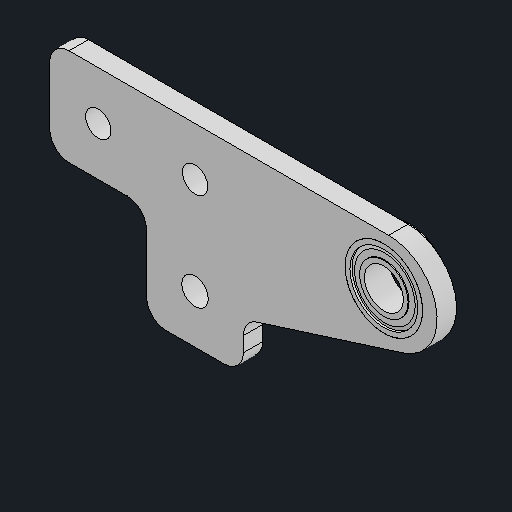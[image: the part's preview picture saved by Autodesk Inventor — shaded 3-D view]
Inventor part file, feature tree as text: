
AUTODESK INVENTOR PART (.ipt)
format: ipt  version: 2024.2 (Build 282272000, 272)  size: 135,168 bytes
history: native  units: mm
features: other x3, fillet x1
ambient origin geometry x8: Origin, YZ Plane, XZ Plane, XY Plane, X Axis, Y Axis, Z Axis, Center Point
bodies: Body1 (feature_tree), Body2 (feature_tree)
feature tree (4):
  other  "솔리드1"
  other  "솔리드2"
  fillet  "Fillet1"  [1 undecoded]
  other  "Cut-Revolve1"
note: 1 required parameter value undecoded (feature->parameter linkage not recoverable at this tier; creation-order binding heuristic only, values carry confidence <= 0.55)
